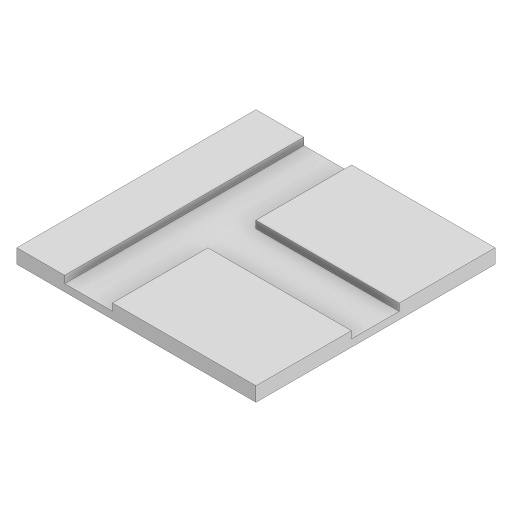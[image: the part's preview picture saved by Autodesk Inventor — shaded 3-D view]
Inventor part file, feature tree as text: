
AUTODESK INVENTOR PART (.ipt)
format: ipt  version: 2023 (Build 270158000, 158)  size: 122,368 bytes
history: native  units: in
note: dims shown in document units (in); Inventor stores cm internally (conversion verified against a paired STEP export)
features: extrude x2, sketch x2, projected_geometry x1
ambient origin geometry x8: Origin, YZ Plane, XZ Plane, XY Plane, X Axis, Y Axis, Z Axis, Center Point
bodies: Solid1 (feature_tree)
feature tree (5):
  extrude  "Extrusion1"  Depth=3937.0079in
  extrude  "Extrusion2"  Depth=2362.2047in
  sketch  "Sketch1"  dims[d0=3937.0079in d1=3937.0079in]
  sketch  "Sketch2"  dims[d2=118.1102in d3=0.0in d4=2362.2047in d5=787.4016in d6=787.4016in d7=118.1102in d8=0.0in]
  projected_geometry  "Projected Loop1"
